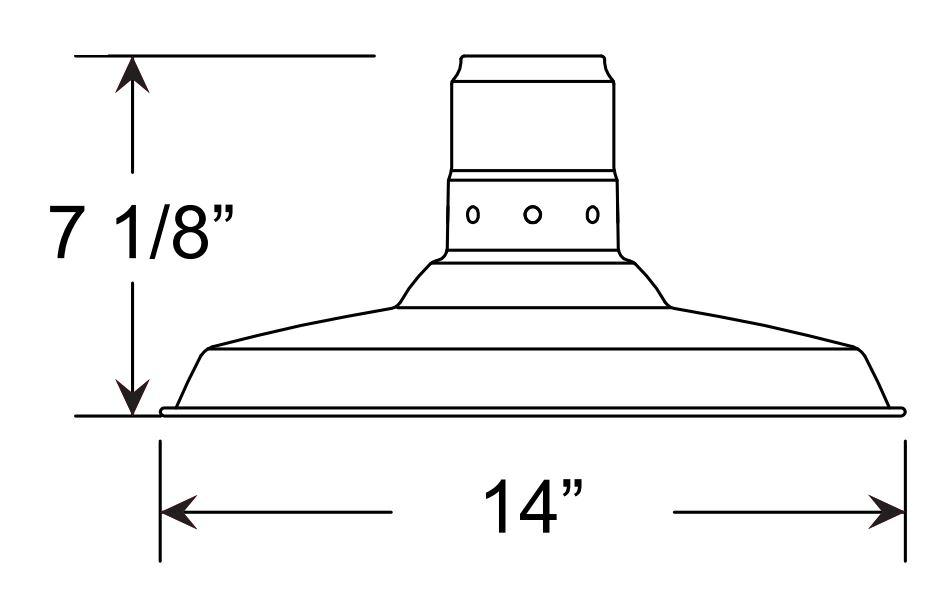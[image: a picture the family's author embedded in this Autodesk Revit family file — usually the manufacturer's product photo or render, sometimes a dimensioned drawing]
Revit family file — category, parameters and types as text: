
# Revit family: Deep Bowl MB
name_source: partatom
category: Lighting Fixtures
units: mm (PartAtom-declared; Revit-internal decimal feet)

## family parameters
Always vertical = Yes
Cut with Voids When Loaded = No
Light Source = Yes
OmniClass Number = 23.80.70.00
OmniClass Title = Lighting
Part Type = Normal
Room Calculation Point = No
Round Connector Dimension = Use Diameter
Shared = No
Work Plane-Based = No

## types (9) — shared parameters
BULB = Yes
Body Colour = Spun aluminium
Body Material = body
CRI = >90
Color Filter = 16777215
Construction Material = Heavy Duty spun aluminum.
Default Elevation = 0' - 0"
Description = 120-277 Voltage
Dimming = 1%
Dimming Lamp Color Temperature Shift = <None>
Efficiency = 65-125 lumens per watt
Lamp = MB
Life = L70 50,000 hours
Load Classification = Lighting
Manufacturer = ANP Lighting
Power Factor = 1
Tilt Angle = 90.00°
URL = https://www.anplighting.com
Voltage = 277 V
Warranty = 5 year limited warranty
b = 0' - 3"

## per-type parameters (varying)
| type | Apparent Load | Bulb | D608 | D610 | D612 | D616 | D618 | Fixture Diameter | Fixture Height | OSD622 | OSD626 | OSD630 | OSD638 | Photometric Web File | Wattage Comments | Weight | a |
| D608 | 100 VA | <By Category> | Yes | No | No | No | No | 0' - 8" | 0' - 7 1/2" | No | No | No | No | D608M009LDNW40K (1).IES | 100 w Max | 1.0lbs | 0' - 8" |
| D610 | 200 VA | <By Category> | No | Yes | No | No | No | 0' - 10 1/4" | 0' - 9 1/4" | No | No | No | No | D610M010LDDW40K.IES | 200 w Max | 1.0lbs | 0' - 9" |
| D612 | 200 VA | <By Category> | No | No | Yes | No | No | 1' - 0" | 0' - 11" | No | No | No | No | D612-100GLCL-32WPL.IES | 200 w Max | 1.0lbs | 0' - 10" |
| D616 | 200 VA | <By Category> | No | No | No | Yes | No | 1' - 4" | 1' - 1 1/4" | No | No | No | No | D616M016LDNW40K (1).IES | 200 w Max | 1.5lbs | 0' - 10" |
| D618 | 200 VA | <By Category> | No | No | No | No | Yes | 1' - 4" | 1' - 6" | No | No | No | No | D618M010LDNW30K.IES | 200 w Max | 2.5 lbs | 1' - 0" |
| OSD622 | 200 VA | Bulb | No | No | No | No | No | 1' - 8" | 1' - 10" | Yes | No | No | No | D618M016LDNW30K.IES | 200 w Max | 7.5lbs | 1' - 3" |
| OSD630 | 200 VA | Bulb | No | No | No | No | No | 2' - 6" | 2' - 3" | No | No | Yes | No | D618M016LDNW30K.IES | 200 w Max | 13.0 lbs | 1' - 7" |
| OSD638 | 200 VA | Bulb | No | No | No | No | No | 3' - 2" | 2' - 7" | No | No | No | Yes | D618M016LDNW30K.IES | 200 w Max | 25.0 lbs | 1' - 6" |
| OSD626 | 200 VA | Bulb | No | No | No | No | No | 2' - 2" | 1' - 11" | No | Yes | No | No | D618M016LDNW30K.IES | 200 w Max | 4.0 lbs | 1' - 3" |

note: column(s) folded — value = type name in every type: Model

## geometry (parser evidence)
native form markers: Sweep x68
no freeform markers — native parametric forms only
